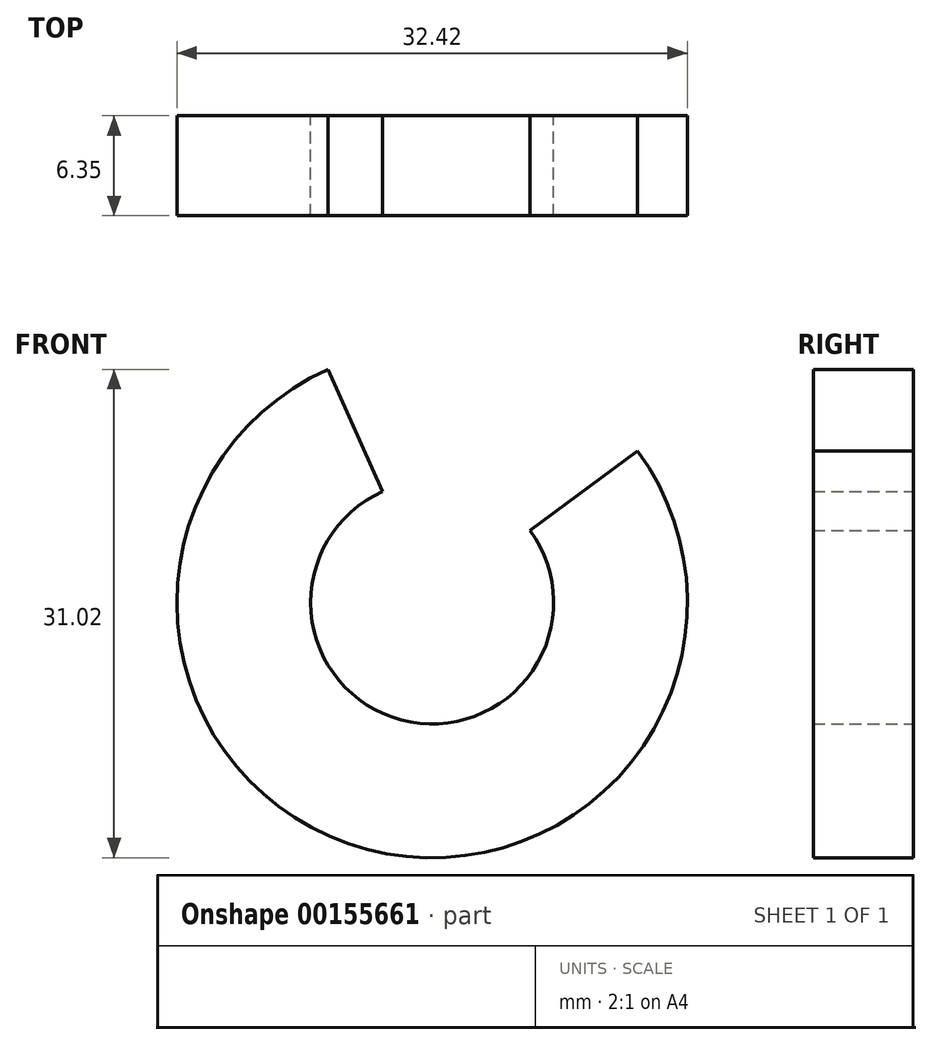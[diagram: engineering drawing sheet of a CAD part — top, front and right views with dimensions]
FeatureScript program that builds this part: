
annotation { "Feature Type Name" : "Feature", "Feature Type Description" : "" }
export const myFeature = defineFeature(function(context is Context, id is Id, definition is map)
    precondition{}
    {
        {
            var Q0;
            Q0=qCreatedBy(makeId("Front.planeOp"),FACE);
            var sketch = newSketch(context, id + "F0", { "sketchPlane" : qUnion([Q0])});
            skCircle(sketch, "E0", {"center": v(0, 0) * mm, "radius": 16.21 * mm});
            skCircle(sketch, "E1", {"center": v(0, 0) * mm, "radius": 7.72 * mm});
            skLineSegment(sketch, "E2", {"start": v(0, 0) * mm, "end": v(-6.6, 14.8) * mm});
            skLineSegment(sketch, "E3", {"start": v(0, 0) * mm, "end": v(13.05, 9.63) * mm});
            skSolve(sketch);
        }
        {
            var Q0;
            {var subQ0=sQuery(id+"F0.wireOp",EDGE,"E2");var subQ1=sQuery(id+"F0.wireOp",EDGE,"E0");var subQ2=makeQuery(id+"F0.imprint","INTERSECT",VERTEX,{"derivedFrom":[subQ1,subQ0]});Q0=makeQuery(id+"F0.imprint","IMPRINT",FACE,{"disambiguationData":[TD([[makeQuery(id+"F0.imprint","IMPRINT",EDGE,{"disambiguationData":[TD([[subQ2,-1.0]])],"derivedFrom":subQ1}),1.0]])]});}
            extrude(context, id + "F1", {"entities" : qUnion([Q0]), "depth" : 6.35 * mm});
        }
    });
